FCSTD DOCUMENT  (FreeCAD 2020.12.08R23076 +2912 (Git))
Label: Modular Ramp v3 Draft
License: All rights reserved
LicenseURL: http://en.wikipedia.org/wiki/All_rights_reserved
objects: App::FeaturePython×4, Part::Part2DObjectPython×1
note: 1 computed .brp shape members not serialized (recipe doc carries the construction recipe); baked Part::Feature solids carry a one-line shape summary decoded from their .brp

FEATURE [Part::Part2DObjectPython] Wire  # Draft 2D object (typed FeaturePython)
  Area = 1500
  ChamferSize = 0
  Closed = true
  End = (100,6.1e-15,0)
  FilletRadius = 0
  Length = 231.98
  MakeFace = true
  Points = (4) [(0,0,0),(1.53081e-16,5,0),(100,25,0),(100,3.06162e-15,0)]
  Start = (0,0,0)
  Subdivisions = 0
FEATURE [App::FeaturePython] Dimension  # Draft dimension (typed FeaturePython)
  Diameter = false
  Dimline = (111,12,0)
  Direction = (0,0,0)
  Distance = 25
  End = (100,6.1e-15,0)
  Normal = (0,0,1)
  Start = (100,25,0)
FEATURE [App::FeaturePython] Dimension001  # Draft dimension (typed FeaturePython)
  Diameter = false
  Dimline = (74,-8,0)
  Direction = (0,0,0)
  Distance = 100
  End = (100,6.1e-15,0)
  Normal = (0,0,1)
  Start = (0,0,0)
FEATURE [App::FeaturePython] Dimension002  # Draft dimension (typed FeaturePython)
  Diameter = false
  Dimline = (-4,2,0)
  Direction = (0,0,0)
  Distance = 5
  End = (0,0,0)
  Normal = (0,0,1)
  Start = (0,5,0)
FEATURE [App::FeaturePython] Dimension003  # Draft dimension (typed FeaturePython)
  Diameter = false
  Dimline = (107.426,-0.19805,0)
  Direction = (0,0,0)
  Distance = 24.6825
  End = (100.021,0.0923278,0)
  Normal = (0,0,1)
  Start = (100.166,24.7744,0)
